# Revit family: result
name_source: partatom
category: Mechanical Equipment
units: mm (PartAtom-declared; Revit-internal decimal feet)

## family parameters
Always vertical = No
Cut with Voids When Loaded = No
Maintain Annotation Orientation = No
OmniClass Number = 23.75.10.00
OmniClass Title = Transformation and Conversion of Energy
Part Type = Normal
Room Calculation Point = No
Round Connector Dimension = Use Radius
Shared = No
Work Plane-Based = No

## types (1)
- -1-NEMBUS 210 R8  - Heat Recovery Units
    Autor = BIM6D
    Aux.PE = 120 mm  [stored 0.393701 ft]
    CorrienteNominal = 0 A
    Default Elevation = 0 mm  [stored 0 ft]
    Description = Domestic MVHR unit with high efficiency counterflow heat exchanger (up to 92%) and low consumption EC motors. The unit assures a continuous and balanced ventilation system, extracting moist stale air from the wet rooms and at the same time introducing a tempered and filtered fresh air to the habitable rooms.The optimized design allows compliance with the highest standards assuring a very low leakage level, high thermal insulation and a minimal sound level. The integrated humidity sensor allows an automatic function tracking the indoor humidity and proportionally adjusting the fans speed.Inlet/extraction filter G4 (ISO coarse 65%, at 140 m3 /h), F7 (ISO ePM1 70%, at 140 m3 /h). Option, M5 (ISO ePM10 50%, at 140 m3 /h). An integrated 100% bypass is activated either automatically or manually. The bypass is particularly useful when the indoors temperature is higher than outdoors and free cooling is preferable.The NEMBUS 210 R8  S&amp;P works at flow 200 m³/h and preasure 100 Pa.
    DiametroImpulsor = 0 mm  [stored 0 ft]
    Flow Drain = 0.0 L/s
    IfcExportAs = IfcAirToAirHeatRecoveryType
    IfcExportType = FIXEDPLATECROSSFLOWEXCHANGER
    IndiceFlujoNominal = 0.0 L/s
    IndicePotenciaNominal = 0 W
    Manufacturer = S&P Sistemas de Ventilación S.L.U.
    MasterformatCodigo = 23 72 00
    MasterformatTitulo = Air-to-Air Energy Recovery Equipment
    Material Carcasa = SP_Plastic_Formed white
    Material Conector Bornes = SP_Plastic_Black
    NumeroPolos = 1
    OmniclassCodigo = 23.75.10.00
    OmniclassTitulo = Transformation and Conversion of Energy
    PA = 1223 mm  [stored 4.01247 ft]
    PB = 1252 mm  [stored 4.10761 ft]
    PC = 694 mm  [stored 2.2769 ft]
    PD = 622 mm  [stored 2.04068 ft]
    PE = 125 mm  [stored 0.410105 ft]
    PF = 264 mm  [stored 0.866142 ft]
    PG = 20 mm  [stored 0.0656168 ft]
    PH = 122 mm  [stored 0.400262 ft]
    PII = 144 mm  [stored 0.472441 ft]
    PJ = 396 mm  [stored 1.29921 ft]
    PK = 147 mm  [stored 0.482283 ft]
    PL = 134 mm
    PM = 122 mm  [stored 0.400262 ft]
    PN = 141 mm
    PO = 391 mm
    PP = 158 mm
    PR = 235 mm  [stored 0.770997 ft]
    PS = 270 mm  [stored 0.885827 ft]
    PT = 16 mm  [stored 0.0524934 ft]
    PU = 9 mm  [stored 0.0295276 ft]
    PesoBruto = 0.00 kg
    PowerFactor = 0.00%
    PresionDinamica = 0.0 Pa
    PresionEstaticaNominal = 0.0 Pa
    PresionTotalNominal = 0.0 Pa
    Radius Connector 1 = 63 mm
    TensionNominal = 0 V
    Type Image = <None>
    UNSPSCCodigo = 72151204
    UNSPSCTitulo = HVAC ventilation and duct work construction service
    URL = https://www.solerpalau.com
    URLProducto = https://www.solerpalau.com
    Uniclass2.0Codigo = Pr_60_60_36
    Uniclass2.0Titulo = Heat recovery distribution equipment
    spIntensidadMaximaAbsorbida = 0 A
    spPotenciaElectrica_Solucion = 0 W
    spPotenciaUtil_Solucion = 0 W
    spTamañoVentilador = 0 mm  [stored 0 ft]

note: [stored X ft] marks values corroborated as IEEE doubles in the binary element streams (Revit-internal decimal feet)
